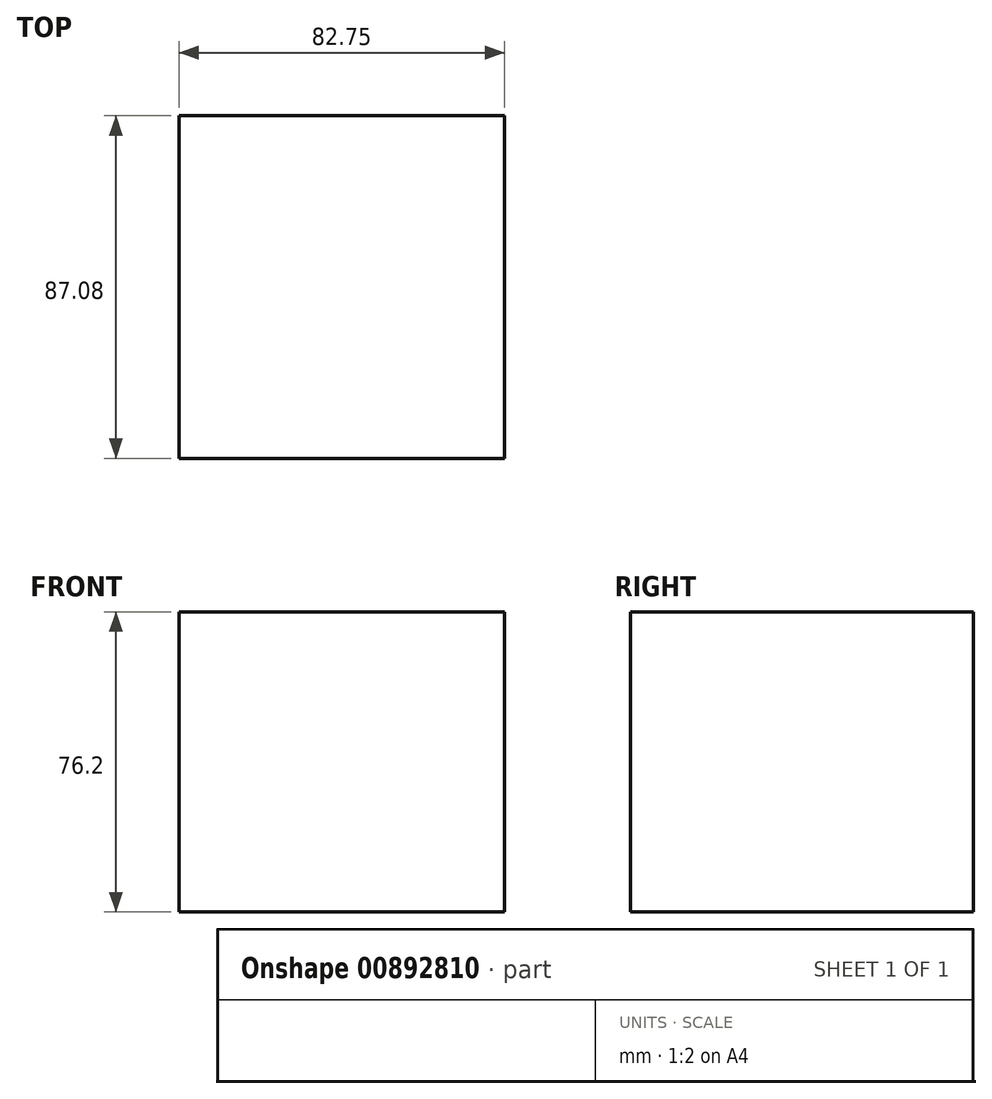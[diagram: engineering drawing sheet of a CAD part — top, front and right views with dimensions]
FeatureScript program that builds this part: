
annotation { "Feature Type Name" : "Feature", "Feature Type Description" : "" }
export const myFeature = defineFeature(function(context is Context, id is Id, definition is map)
    precondition{}
    {
        {
            var Q0;
            Q0=qCreatedBy(makeId("Top.planeOp"),FACE);
            var sketch = newSketch(context, id + "F0", { "sketchPlane" : qUnion([Q0])});
            skLineSegment(sketch, "E0.bottom", {"start": v(40.46, -38.7) * mm, "end": v(-42.29, -38.7) * mm});
            skLineSegment(sketch, "E0.top", {"start": v(40.46, 48.4) * mm, "end": v(-42.29, 48.4) * mm});
            skLineSegment(sketch, "E0.left", {"start": v(40.46, -38.7) * mm, "end": v(40.46, 48.4) * mm});
            skLineSegment(sketch, "E0.right", {"start": v(-42.29, -38.7) * mm, "end": v(-42.29, 48.4) * mm});
            skSolve(sketch);
        }
        {
            var Q0;
            Q0 = qSketchRegion(id + "F0", true);
            extrude(context, id + "F1", {"entities" : qUnion([Q0]), "depth" : 76.2 * mm, "offsetDistance" : 25.4 * mm});
        }
    });
